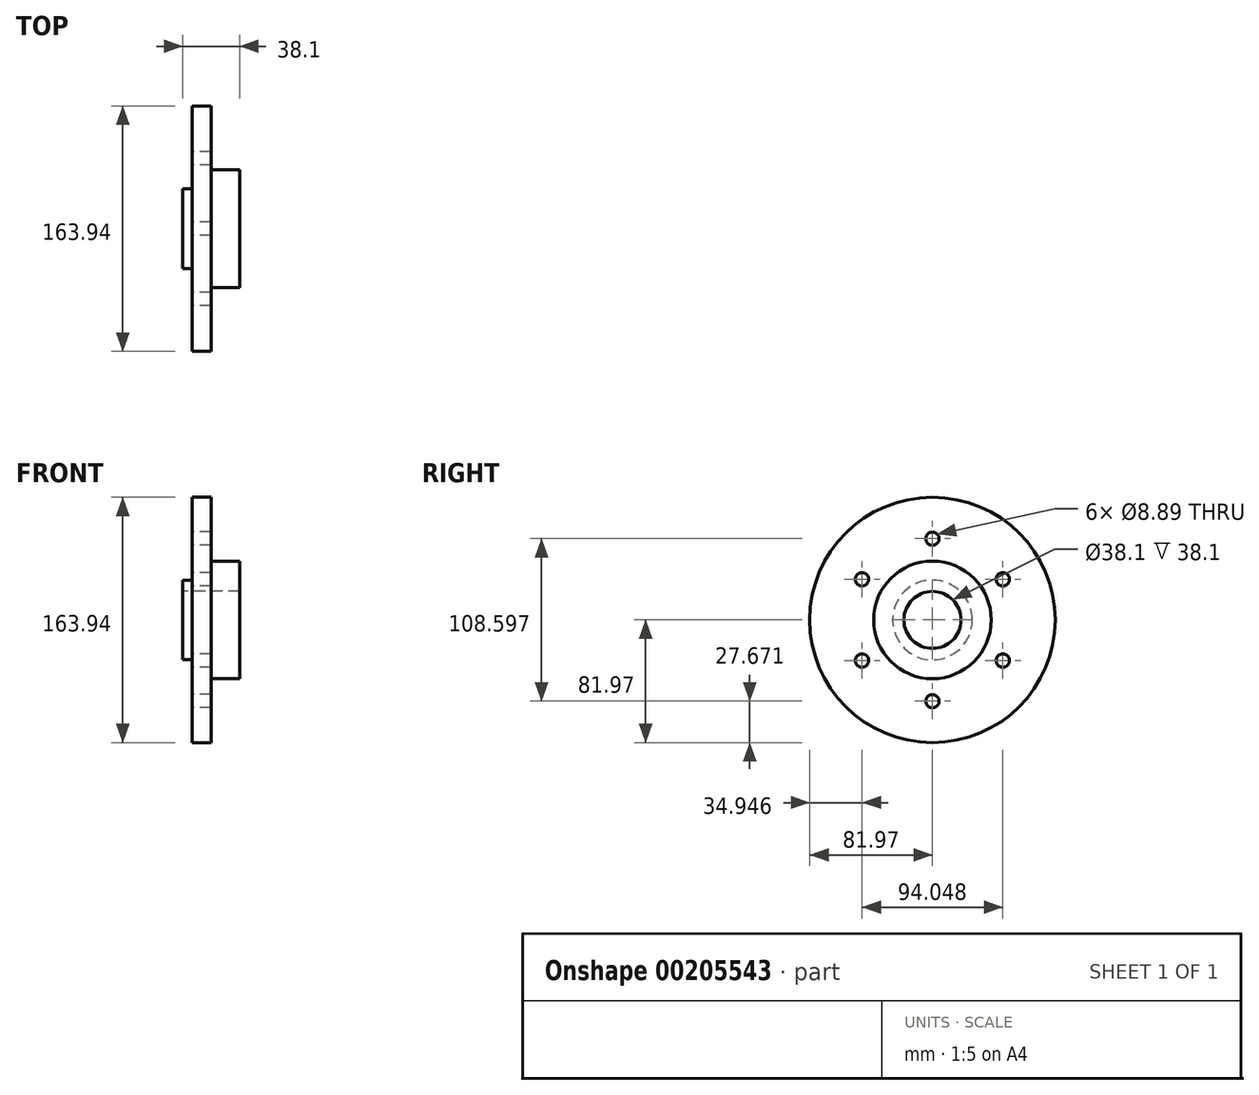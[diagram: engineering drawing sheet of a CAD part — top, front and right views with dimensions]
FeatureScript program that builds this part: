
annotation { "Feature Type Name" : "Feature", "Feature Type Description" : "" }
export const myFeature = defineFeature(function(context is Context, id is Id, definition is map)
    precondition{}
    {
        {
            var Q0;
            Q0=qCreatedBy(makeId("Front.planeOp"),FACE);
            var sketch = newSketch(context, id + "F0", { "sketchPlane" : qUnion([Q0])});
            skLineSegment(sketch, "E0", {"start": v(-89.12, 0) * mm, "end": v(94.02, 0) * mm, "construction": true});
            skLineSegment(sketch, "E1", {"start": v(0, 19.05) * mm, "end": v(38.1, 19.05) * mm});
            skLineSegment(sketch, "E2", {"start": v(38.1, 19.05) * mm, "end": v(38.1, 39.29) * mm});
            skLineSegment(sketch, "E3", {"start": v(38.1, 39.29) * mm, "end": v(19.05, 39.29) * mm});
            skLineSegment(sketch, "E4", {"start": v(19.05, 39.29) * mm, "end": v(19.05, 81.97) * mm});
            skLineSegment(sketch, "E5", {"start": v(19.05, 81.97) * mm, "end": v(6.35, 81.97) * mm});
            skLineSegment(sketch, "E6", {"start": v(6.35, 81.97) * mm, "end": v(6.35, 26.63) * mm});
            skLineSegment(sketch, "E7", {"start": v(6.35, 26.63) * mm, "end": v(0, 26.63) * mm});
            skLineSegment(sketch, "E8", {"start": v(0, 26.63) * mm, "end": v(0, 19.05) * mm});
            skPoint(sketch, "E9", {"position": v(6.35, 54.3) * mm});
            skSolve(sketch);
        }
        {
            var Q0;
            Q0=makeQuery(id+"F0.imprint","IMPRINT",FACE,{"disambiguationData":[TD([[makeQuery(id+"F0.imprint","IMPRINT",EDGE,{"derivedFrom":sQuery(id+"F0.wireOp",EDGE,"E1")}),1.0]])]});
            var Q1;
            Q1=sQuery(id+"F0.wireOp",EDGE,"E0");
            revolve(context, id + "F1", {"entities" : qUnion([Q0]), "axis" : qUnion([Q1]), "revolveType" : RevolveType.FULL});
        }
        {
            var Q0;
            Q0=makeQuery(id+"F1.opRevolve","SWEPT_FACE",FACE,{"disambiguationData":[OSD([sQuery(id+"F0.wireOp",EDGE,"E6")])]});
            var Q1;
            Q1=qBodyType(qCreatedBy(id+"F3",EDGE),BodyType.WIRE);
            cPlane(context, id + "F2", {"entities" : qUnion([Q0, Q1]), "cplaneType" : CPlaneType.OFFSET, "offset" : 0 * mm, "width" : 152.4 * mm, "height" : 152.4 * mm});
        }
        {
            var Q0;
            Q0=qCreatedBy(id+"F2.planeOp",FACE);
            var sketch = newSketch(context, id + "F3", { "sketchPlane" : qUnion([Q0])});
            skCircle(sketch, "E10", {"center": v(0, 0) * mm, "radius": 54.3 * mm, "construction": true});
            skCircle(sketch, "E11", {"center": v(0, 54.3) * mm, "radius": 4.45 * mm});
            skCircle(sketch, "E12.1.0", {"center": v(-47.02, 27.15) * mm, "radius": 4.45 * mm});
            skCircle(sketch, "E12.2.0", {"center": v(-47.02, -27.15) * mm, "radius": 4.45 * mm});
            skCircle(sketch, "E12.3.0", {"center": v(0, -54.3) * mm, "radius": 4.45 * mm});
            skCircle(sketch, "E12.4.0", {"center": v(47.02, -27.15) * mm, "radius": 4.45 * mm});
            skCircle(sketch, "E12.5.0", {"center": v(47.02, 27.15) * mm, "radius": 4.45 * mm});
            skSolve(sketch);
        }
        {
            var Q0;
            Q0=makeQuery(id+"F3.imprint","IMPRINT",FACE,{"disambiguationData":[TD([[makeQuery(id+"F3.imprint","IMPRINT",EDGE,{"derivedFrom":sQuery(id+"F3.wireOp",EDGE,"E11")}),1.0]])]});
            var Q1;
            Q1=makeQuery(id+"F3.imprint","IMPRINT",FACE,{"disambiguationData":[TD([[makeQuery(id+"F3.imprint","IMPRINT",EDGE,{"derivedFrom":sQuery(id+"F3.wireOp",EDGE,"E12.1.0")}),1.0]])]});
            var Q2;
            Q2=makeQuery(id+"F3.imprint","IMPRINT",FACE,{"disambiguationData":[TD([[makeQuery(id+"F3.imprint","IMPRINT",EDGE,{"derivedFrom":sQuery(id+"F3.wireOp",EDGE,"E12.2.0")}),1.0]])]});
            var Q3;
            Q3=makeQuery(id+"F3.imprint","IMPRINT",FACE,{"disambiguationData":[TD([[makeQuery(id+"F3.imprint","IMPRINT",EDGE,{"derivedFrom":sQuery(id+"F3.wireOp",EDGE,"E12.3.0")}),1.0]])]});
            var Q4;
            Q4=makeQuery(id+"F3.imprint","IMPRINT",FACE,{"disambiguationData":[TD([[makeQuery(id+"F3.imprint","IMPRINT",EDGE,{"derivedFrom":sQuery(id+"F3.wireOp",EDGE,"E12.4.0")}),1.0]])]});
            var Q5;
            Q5=makeQuery(id+"F3.imprint","IMPRINT",FACE,{"disambiguationData":[TD([[makeQuery(id+"F3.imprint","IMPRINT",EDGE,{"derivedFrom":sQuery(id+"F3.wireOp",EDGE,"E12.5.0")}),1.0]])]});
            extrude(context, id + "F4", {"entities" : qUnion([Q0, Q1, Q2, Q3, Q4, Q5]), "operationType" : NewBodyOperationType.REMOVE, "endBound" : BoundingType.THROUGH_ALL, "oppositeDirection" : true, "depth" : 25.4 * mm});
        }
    });
